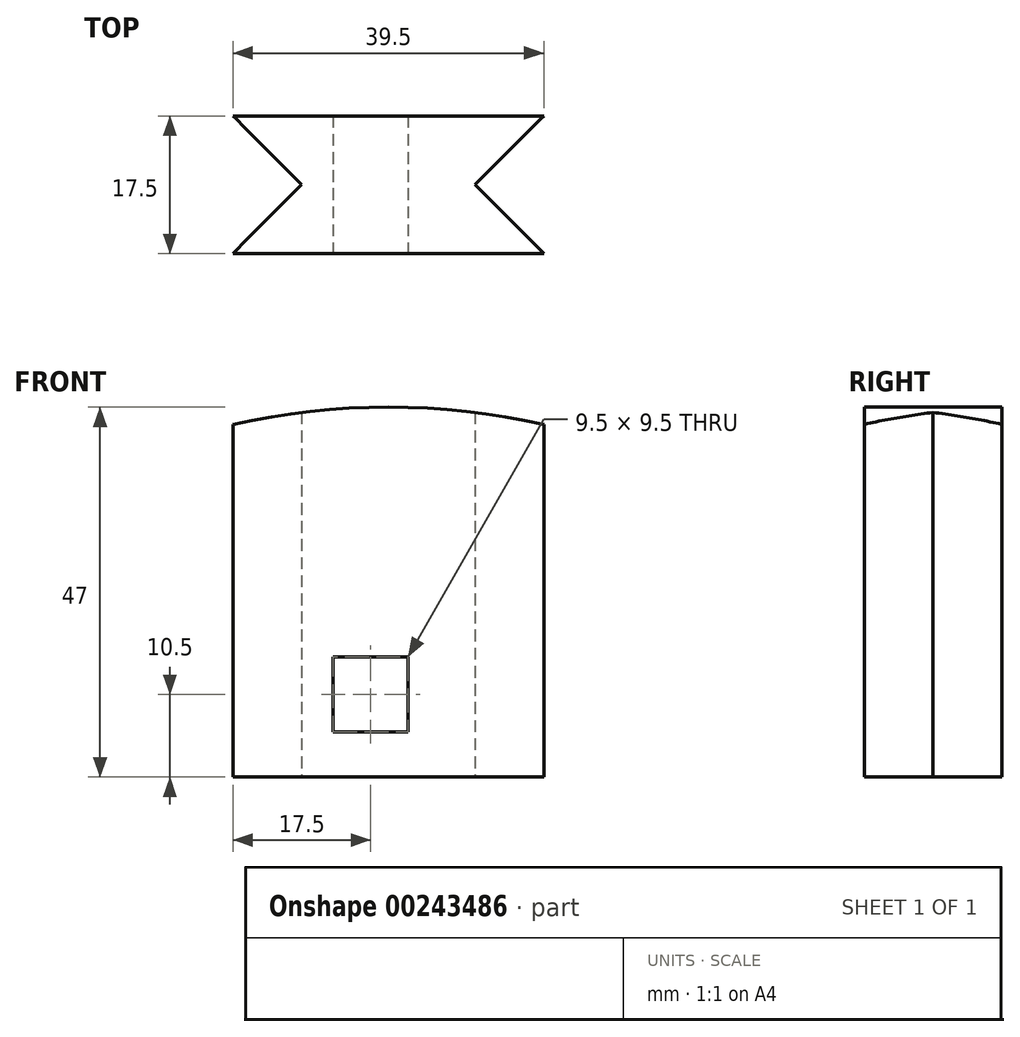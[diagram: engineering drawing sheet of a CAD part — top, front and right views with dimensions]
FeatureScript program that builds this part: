
annotation { "Feature Type Name" : "Feature", "Feature Type Description" : "" }
export const myFeature = defineFeature(function(context is Context, id is Id, definition is map)
    precondition{}
    {
        {
            var Q0;
            Q0=qCreatedBy(makeId("Top.planeOp"),FACE);
            var sketch = newSketch(context, id + "F0", { "sketchPlane" : qUnion([Q0])});
            skLineSegment(sketch, "E0.bottom", {"start": v(0, 0) * mm, "end": v(39.5, 0) * mm});
            skLineSegment(sketch, "E0.top", {"start": v(0, 17.5) * mm, "end": v(39.5, 17.5) * mm});
            skLineSegment(sketch, "E0.left", {"start": v(0, 0) * mm, "end": v(0, 17.5) * mm});
            skLineSegment(sketch, "E0.right", {"start": v(39.5, 0) * mm, "end": v(39.5, 17.5) * mm});
            skLineSegment(sketch, "E1", {"start": v(0, 0) * mm, "end": v(8.75, 8.75) * mm});
            skLineSegment(sketch, "E2", {"start": v(8.75, 8.75) * mm, "end": v(0, 17.5) * mm});
            skLineSegment(sketch, "E3", {"start": v(39.5, 0) * mm, "end": v(30.75, 8.75) * mm});
            skLineSegment(sketch, "E4", {"start": v(30.75, 8.75) * mm, "end": v(39.5, 17.5) * mm});
            skSolve(sketch);
        }
        {
            var Q0;
            Q0=makeQuery(id+"F0.imprint","IMPRINT",FACE,{"disambiguationData":[TD([[makeQuery(id+"F0.imprint","IMPRINT",EDGE,{"derivedFrom":sQuery(id+"F0.wireOp",EDGE,"E0.bottom")}),1.0]])]});
            extrude(context, id + "F1", {"entities" : qUnion([Q0]), "depth" : 47 * mm, "offsetDistance" : 25 * mm});
        }
        {
            var Q0;
            Q0=makeQuery(id+"F1.opExtrude","SWEPT_FACE",FACE,{"disambiguationData":[OSD([sQuery(id+"F0.wireOp",EDGE,"E0.bottom")])]});
            var sketch = newSketch(context, id + "F2", { "sketchPlane" : qUnion([Q0])});
            skArc(sketch, "E5", {"start": v(42.47, 44.08) * mm, "mid": v(18.36, 46.99) * mm, "end": v(-5.64, 43.34) * mm});
            skLineSegment(sketch, "E6", {"start": v(-5.64, 43.34) * mm, "end": v(-5.64, 47.1) * mm});
            skLineSegment(sketch, "E7", {"start": v(-5.64, 47.1) * mm, "end": v(45.14, 47.1) * mm});
            skLineSegment(sketch, "E8", {"start": v(45.14, 47.1) * mm, "end": v(42.47, 44.08) * mm});
            skLineSegment(sketch, "E9", {"start": v(-5.64, 47.1) * mm, "end": v(19.75, -42.9) * mm, "construction": true});
            skLineSegment(sketch, "E10", {"start": v(45.14, 47.1) * mm, "end": v(19.75, -42.9) * mm, "construction": true});
            skLineSegment(sketch, "E11", {"start": v(-5.64, 47.1) * mm, "end": v(0, 0) * mm, "construction": true});
            skLineSegment(sketch, "E12", {"start": v(45.14, 47.1) * mm, "end": v(39.5, 0) * mm, "construction": true});
            skSolve(sketch);
        }
        {
            var Q0;
            Q0 = qSketchRegion(id + "F2", true);
            extrude(context, id + "F3", {"entities" : qUnion([Q0]), "operationType" : NewBodyOperationType.REMOVE, "oppositeDirection" : true, "depth" : 25 * mm, "offsetDistance" : 25 * mm});
        }
        {
            var Q0;
            Q0=makeQuery(id+"F1.opExtrude","SWEPT_FACE",FACE,{"disambiguationData":[OSD([sQuery(id+"F0.wireOp",EDGE,"E0.bottom")])]});
            var sketch = newSketch(context, id + "F4", { "sketchPlane" : qUnion([Q0])});
            skLineSegment(sketch, "E13.bottom", {"start": v(12.75, 5.75) * mm, "end": v(22.25, 5.75) * mm});
            skLineSegment(sketch, "E13.top", {"start": v(12.75, 15.25) * mm, "end": v(22.25, 15.25) * mm});
            skLineSegment(sketch, "E13.left", {"start": v(12.75, 5.75) * mm, "end": v(12.75, 15.25) * mm});
            skLineSegment(sketch, "E13.right", {"start": v(22.25, 5.75) * mm, "end": v(22.25, 15.25) * mm});
            skSolve(sketch);
        }
        {
            var Q0;
            Q0 = qSketchRegion(id + "F4", true);
            extrude(context, id + "F5", {"entities" : qUnion([Q0]), "operationType" : NewBodyOperationType.REMOVE, "oppositeDirection" : true, "depth" : 25 * mm, "offsetDistance" : 25 * mm});
        }
    });
